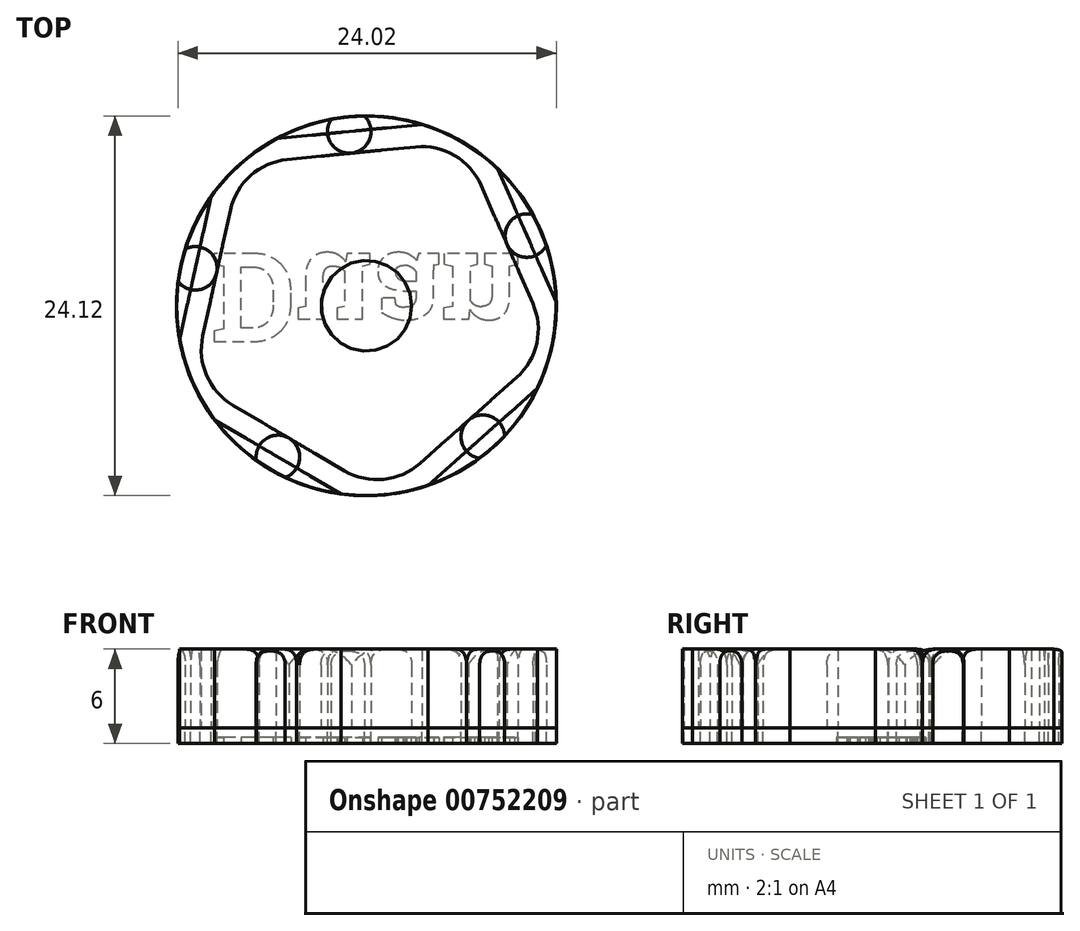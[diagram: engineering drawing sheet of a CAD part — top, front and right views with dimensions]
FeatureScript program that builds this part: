
annotation { "Feature Type Name" : "Feature", "Feature Type Description" : "" }
export const myFeature = defineFeature(function(context is Context, id is Id, definition is map)
    precondition{}
    {
        {
            var Q0;
            Q0=qCreatedBy(makeId("Top.planeOp"),FACE);
            var sketch = newSketch(context, id + "F0", { "sketchPlane" : qUnion([Q0])});
            skCircle(sketch, "E0", {"center": v(-4.76, 4.72) * mm, "radius": 4.1 * mm});
            skCircle(sketch, "E1.1.0", {"center": v(-6.51, -3.29) * mm, "radius": 4.1 * mm});
            skCircle(sketch, "E1.2.0", {"center": v(0.56, -7.43) * mm, "radius": 4.1 * mm});
            skCircle(sketch, "E1.3.0", {"center": v(6.7, -1.99) * mm, "radius": 4.1 * mm});
            skCircle(sketch, "E1.4.0", {"center": v(3.4, 5.53) * mm, "radius": 4.1 * mm});
            skPoint(sketch, "E1.center", {"position": v(-0.12, -0.5) * mm});
            skCircle(sketch, "E2", {"center": v(-0.12, -0.5) * mm, "radius": 12.06 * mm});
            skLineSegment(sketch, "E3", {"start": v(5.82, 8.84) * mm, "end": v(6.43, 9.63) * mm, "construction": true});
            skCircle(sketch, "E4", {"center": v(-0.12, -0.5) * mm, "radius": 2.88 * mm});
            skLineSegment(sketch, "E5", {"start": v(-8.58, -6.83) * mm, "end": v(-1.5, -10.97) * mm});
            skLineSegment(sketch, "E6", {"start": v(-9.76, -7.74) * mm, "end": v(-1.73, -12.44) * mm});
            skLineSegment(sketch, "E7.1.0", {"start": v(3.8, -11.9) * mm, "end": v(10.75, -5.72) * mm});
            skLineSegment(sketch, "E7.1.1", {"start": v(3.29, -10.5) * mm, "end": v(9.42, -5.05) * mm});
            skLineSegment(sketch, "E7.2.0", {"start": v(11.93, -0.3) * mm, "end": v(8.2, 8.23) * mm});
            skLineSegment(sketch, "E7.2.1", {"start": v(10.45, -0.34) * mm, "end": v(7.16, 7.17) * mm});
            skLineSegment(sketch, "E7.3.0", {"start": v(3.42, 11.04) * mm, "end": v(-5.84, 10.12) * mm});
            skLineSegment(sketch, "E7.3.1", {"start": v(3, 9.6) * mm, "end": v(-5.16, 8.8) * mm});
            skLineSegment(sketch, "E7.4.0", {"start": v(-10, 6.43) * mm, "end": v(-11.98, -2.66) * mm});
            skLineSegment(sketch, "E7.4.1", {"start": v(-8.76, 5.6) * mm, "end": v(-10.52, -2.41) * mm});
            skCircle(sketch, "E8", {"center": v(-5.75, -10.1) * mm, "radius": 1.38 * mm});
            skCircle(sketch, "E9.1.0", {"center": v(7.27, -8.8) * mm, "radius": 1.38 * mm});
            skCircle(sketch, "E9.2.0", {"center": v(10.07, 3.97) * mm, "radius": 1.38 * mm});
            skCircle(sketch, "E9.3.0", {"center": v(-1.21, 10.58) * mm, "radius": 1.38 * mm});
            skCircle(sketch, "E9.4.0", {"center": v(-10.99, 1.89) * mm, "radius": 1.38 * mm});
            skSolve(sketch);
        }
        {
            var Q0;
            {var subQ0=sQuery(id+"F0.wireOp",EDGE,"E8");var subQ1=sQuery(id+"F0.wireOp",EDGE,"E2");var subQ2=makeQuery(id+"F0.imprint","INTERSECT",VERTEX,{"disambiguationData":[OD(0.0)],"derivedFrom":[subQ1,subQ0]});Q0=makeQuery(id+"F0.imprint","IMPRINT",FACE,{"disambiguationData":[TD([[makeQuery(id+"F0.imprint","IMPRINT",EDGE,{"disambiguationData":[TD([[subQ2,-1.0]])],"derivedFrom":subQ1}),1.0]])]});}
            var Q1;
            {var subQ5=sQuery(id+"F0.wireOp",EDGE,"E7.1.1");var subQ6=sQuery(id+"F0.wireOp",EDGE,"E1.3.0");var subQ7=makeQuery(id+"F0.imprint","INTERSECT",VERTEX,{"derivedFrom":[subQ6,subQ5]});Q1=makeQuery(id+"F0.imprint","IMPRINT",FACE,{"disambiguationData":[TD([[makeQuery(id+"F0.imprint","IMPRINT",EDGE,{"disambiguationData":[TD([[subQ7,-1.0]])],"derivedFrom":subQ6}),-1.0]])]});}
            var Q2;
            {var subQ0=sQuery(id+"F0.wireOp",EDGE,"E7.1.1");var subQ1=sQuery(id+"F0.wireOp",EDGE,"E1.2.0");var subQ2=makeQuery(id+"F0.imprint","INTERSECT",VERTEX,{"derivedFrom":[subQ1,subQ0]});Q2=makeQuery(id+"F0.imprint","IMPRINT",FACE,{"disambiguationData":[TD([[makeQuery(id+"F0.imprint","IMPRINT",EDGE,{"disambiguationData":[TD([[subQ2,-1.0]])],"derivedFrom":subQ1}),-1.0]])]});}
            var Q3;
            {var subQ0=sQuery(id+"F0.wireOp",EDGE,"E4");var subQ4=makeQuery(id+"F0.imprint","INTERSECT",VERTEX,{"derivedFrom":[sQuery(id+"F0.wireOp",EDGE,"E0"),subQ0]});Q3=makeQuery(id+"F0.imprint","IMPRINT",FACE,{"disambiguationData":[TD([[makeQuery(id+"F0.imprint","IMPRINT",EDGE,{"disambiguationData":[TD([[subQ4,1.0]])],"derivedFrom":subQ0}),1.0]])]});}
            var Q4;
            {var subQ0=sQuery(id+"F0.wireOp",EDGE,"E9.4.0");var subQ1=sQuery(id+"F0.wireOp",EDGE,"E7.4.0");var subQ2=makeQuery(id+"F0.imprint","INTERSECT",VERTEX,{"disambiguationData":[OD(0.0)],"derivedFrom":[subQ1,subQ0]});Q4=makeQuery(id+"F0.imprint","IMPRINT",FACE,{"disambiguationData":[TD([[makeQuery(id+"F0.imprint","IMPRINT",EDGE,{"disambiguationData":[TD([[subQ2,-1.0]])],"derivedFrom":subQ1}),1.0]])]});}
            var Q5;
            {var subQ0=sQuery(id+"F0.wireOp",EDGE,"E1.3.0");var subQ1=sQuery(id+"F0.wireOp",EDGE,"E1.2.0");var subQ2=makeQuery(id+"F0.imprint","INTERSECT",VERTEX,{"derivedFrom":[subQ1,subQ0]});Q5=makeQuery(id+"F0.imprint","IMPRINT",FACE,{"disambiguationData":[TD([[makeQuery(id+"F0.imprint","IMPRINT",EDGE,{"disambiguationData":[TD([[subQ2,-1.0]])],"derivedFrom":subQ1}),-1.0]])]});}
            var Q6;
            {var subQ0=sQuery(id+"F0.wireOp",EDGE,"E9.1.0");var subQ1=sQuery(id+"F0.wireOp",EDGE,"E2");var subQ2=makeQuery(id+"F0.imprint","INTERSECT",VERTEX,{"disambiguationData":[OD(0.0)],"derivedFrom":[subQ1,subQ0]});Q6=makeQuery(id+"F0.imprint","IMPRINT",FACE,{"disambiguationData":[TD([[makeQuery(id+"F0.imprint","IMPRINT",EDGE,{"disambiguationData":[TD([[subQ2,-1.0]])],"derivedFrom":subQ1}),1.0]])]});}
            var Q7;
            {var subQ0=sQuery(id+"F0.wireOp",EDGE,"E9.3.0");var subQ1=sQuery(id+"F0.wireOp",EDGE,"E2");var subQ2=makeQuery(id+"F0.imprint","INTERSECT",VERTEX,{"disambiguationData":[OD(0.0)],"derivedFrom":[subQ1,subQ0]});Q7=makeQuery(id+"F0.imprint","IMPRINT",FACE,{"disambiguationData":[TD([[makeQuery(id+"F0.imprint","IMPRINT",EDGE,{"disambiguationData":[TD([[subQ2,-1.0]])],"derivedFrom":subQ1}),1.0]])]});}
            var Q8;
            {var subQ0=sQuery(id+"F0.wireOp",EDGE,"E7.3.1");var subQ1=sQuery(id+"F0.wireOp",EDGE,"E0");var subQ2=makeQuery(id+"F0.imprint","INTERSECT",VERTEX,{"derivedFrom":[subQ1,subQ0]});Q8=makeQuery(id+"F0.imprint","IMPRINT",FACE,{"disambiguationData":[TD([[makeQuery(id+"F0.imprint","IMPRINT",EDGE,{"disambiguationData":[TD([[subQ2,-1.0]])],"derivedFrom":subQ1}),-1.0]])]});}
            var Q9;
            {var subQ0=sQuery(id+"F0.wireOp",EDGE,"E7.3.1");var subQ1=sQuery(id+"F0.wireOp",EDGE,"E0");var subQ2=makeQuery(id+"F0.imprint","INTERSECT",VERTEX,{"derivedFrom":[subQ1,subQ0]});Q9=makeQuery(id+"F0.imprint","IMPRINT",FACE,{"disambiguationData":[TD([[makeQuery(id+"F0.imprint","IMPRINT",EDGE,{"disambiguationData":[TD([[subQ2,1.0]])],"derivedFrom":subQ1}),-1.0]])]});}
            var Q10;
            {var subQ0=sQuery(id+"F0.wireOp",EDGE,"E9.2.0");var subQ1=sQuery(id+"F0.wireOp",EDGE,"E2");var subQ2=makeQuery(id+"F0.imprint","INTERSECT",VERTEX,{"disambiguationData":[OD(0.0)],"derivedFrom":[subQ1,subQ0]});Q10=makeQuery(id+"F0.imprint","IMPRINT",FACE,{"disambiguationData":[TD([[makeQuery(id+"F0.imprint","IMPRINT",EDGE,{"disambiguationData":[TD([[subQ2,-1.0]])],"derivedFrom":subQ1}),1.0]])]});}
            var Q11;
            {var subQ0=sQuery(id+"F0.wireOp",EDGE,"E1.2.0");var subQ1=sQuery(id+"F0.wireOp",EDGE,"E1.1.0");var subQ2=makeQuery(id+"F0.imprint","INTERSECT",VERTEX,{"derivedFrom":[subQ1,subQ0]});Q11=makeQuery(id+"F0.imprint","IMPRINT",FACE,{"disambiguationData":[TD([[makeQuery(id+"F0.imprint","IMPRINT",EDGE,{"disambiguationData":[TD([[subQ2,-1.0]])],"derivedFrom":subQ1}),-1.0]])]});}
            var Q12;
            {var subQ0=sQuery(id+"F0.wireOp",EDGE,"E1.2.0");var subQ4=makeQuery(id+"F0.imprint","INTERSECT",VERTEX,{"derivedFrom":[subQ0,sQuery(id+"F0.wireOp",EDGE,"E5")]});Q12=makeQuery(id+"F0.imprint","IMPRINT",FACE,{"disambiguationData":[TD([[makeQuery(id+"F0.imprint","IMPRINT",EDGE,{"disambiguationData":[TD([[subQ4,1.0]])],"derivedFrom":subQ0}),1.0]])]});}
            var Q13;
            {var subQ0=sQuery(id+"F0.wireOp",EDGE,"E9.1.0");var subQ1=sQuery(id+"F0.wireOp",EDGE,"E7.1.0");var subQ2=makeQuery(id+"F0.imprint","INTERSECT",VERTEX,{"disambiguationData":[OD(0.0)],"derivedFrom":[subQ1,subQ0]});Q13=makeQuery(id+"F0.imprint","IMPRINT",FACE,{"disambiguationData":[TD([[makeQuery(id+"F0.imprint","IMPRINT",EDGE,{"disambiguationData":[TD([[subQ2,-1.0]])],"derivedFrom":subQ1}),1.0]])]});}
            var Q14;
            {var subQ0=sQuery(id+"F0.wireOp",EDGE,"E9.3.0");var subQ1=sQuery(id+"F0.wireOp",EDGE,"E7.3.0");var subQ2=makeQuery(id+"F0.imprint","INTERSECT",VERTEX,{"disambiguationData":[OD(0.0)],"derivedFrom":[subQ1,subQ0]});Q14=makeQuery(id+"F0.imprint","IMPRINT",FACE,{"disambiguationData":[TD([[makeQuery(id+"F0.imprint","IMPRINT",EDGE,{"disambiguationData":[TD([[subQ2,-1.0]])],"derivedFrom":subQ1}),1.0]])]});}
            var Q15;
            {var subQ0=sQuery(id+"F0.wireOp",EDGE,"E1.4.0");var subQ4=makeQuery(id+"F0.imprint","INTERSECT",VERTEX,{"derivedFrom":[subQ0,sQuery(id+"F0.wireOp",EDGE,"E7.2.1")]});Q15=makeQuery(id+"F0.imprint","IMPRINT",FACE,{"disambiguationData":[TD([[makeQuery(id+"F0.imprint","IMPRINT",EDGE,{"disambiguationData":[TD([[subQ4,1.0]])],"derivedFrom":subQ0}),1.0]])]});}
            var Q16;
            {var subQ7=sQuery(id+"F0.wireOp",EDGE,"E5");var subQ8=sQuery(id+"F0.wireOp",EDGE,"E1.2.0");var subQ9=makeQuery(id+"F0.imprint","INTERSECT",VERTEX,{"derivedFrom":[subQ8,subQ7]});Q16=makeQuery(id+"F0.imprint","IMPRINT",FACE,{"disambiguationData":[TD([[makeQuery(id+"F0.imprint","IMPRINT",EDGE,{"disambiguationData":[TD([[subQ9,-1.0]])],"derivedFrom":subQ8}),-1.0]])]});}
            var Q17;
            {var subQ0=sQuery(id+"F0.wireOp",EDGE,"E5");var subQ1=sQuery(id+"F0.wireOp",EDGE,"E1.1.0");var subQ2=makeQuery(id+"F0.imprint","INTERSECT",VERTEX,{"derivedFrom":[subQ1,subQ0]});Q17=makeQuery(id+"F0.imprint","IMPRINT",FACE,{"disambiguationData":[TD([[makeQuery(id+"F0.imprint","IMPRINT",EDGE,{"disambiguationData":[TD([[subQ2,-1.0]])],"derivedFrom":subQ1}),-1.0]])]});}
            var Q18;
            {var subQ0=sQuery(id+"F0.wireOp",EDGE,"E9.4.0");var subQ1=sQuery(id+"F0.wireOp",EDGE,"E2");var subQ2=makeQuery(id+"F0.imprint","INTERSECT",VERTEX,{"disambiguationData":[OD(0.0)],"derivedFrom":[subQ1,subQ0]});Q18=makeQuery(id+"F0.imprint","IMPRINT",FACE,{"disambiguationData":[TD([[makeQuery(id+"F0.imprint","IMPRINT",EDGE,{"disambiguationData":[TD([[subQ2,-1.0]])],"derivedFrom":subQ1}),1.0]])]});}
            var Q19;
            {var subQ0=sQuery(id+"F0.wireOp",EDGE,"E1.4.0");var subQ1=sQuery(id+"F0.wireOp",EDGE,"E0");var subQ2=makeQuery(id+"F0.imprint","INTERSECT",VERTEX,{"derivedFrom":[subQ1,subQ0]});Q19=makeQuery(id+"F0.imprint","IMPRINT",FACE,{"disambiguationData":[TD([[makeQuery(id+"F0.imprint","IMPRINT",EDGE,{"disambiguationData":[TD([[subQ2,1.0]])],"derivedFrom":subQ1}),-1.0]])]});}
            var Q20;
            {var subQ0=sQuery(id+"F0.wireOp",EDGE,"E1.1.0");var subQ1=sQuery(id+"F0.wireOp",EDGE,"E0");var subQ2=makeQuery(id+"F0.imprint","INTERSECT",VERTEX,{"derivedFrom":[subQ1,subQ0]});Q20=makeQuery(id+"F0.imprint","IMPRINT",FACE,{"disambiguationData":[TD([[makeQuery(id+"F0.imprint","IMPRINT",EDGE,{"disambiguationData":[TD([[subQ2,-1.0]])],"derivedFrom":subQ1}),-1.0]])]});}
            var Q21;
            {var subQ0=sQuery(id+"F0.wireOp",EDGE,"E7.2.1");var subQ1=sQuery(id+"F0.wireOp",EDGE,"E1.3.0");var subQ2=makeQuery(id+"F0.imprint","INTERSECT",VERTEX,{"derivedFrom":[subQ1,subQ0]});Q21=makeQuery(id+"F0.imprint","IMPRINT",FACE,{"disambiguationData":[TD([[makeQuery(id+"F0.imprint","IMPRINT",EDGE,{"disambiguationData":[TD([[subQ2,-1.0]])],"derivedFrom":subQ1}),-1.0]])]});}
            var Q22;
            {var subQ0=sQuery(id+"F0.wireOp",EDGE,"E1.1.0");var subQ4=makeQuery(id+"F0.imprint","INTERSECT",VERTEX,{"derivedFrom":[subQ0,sQuery(id+"F0.wireOp",EDGE,"E7.4.1")]});Q22=makeQuery(id+"F0.imprint","IMPRINT",FACE,{"disambiguationData":[TD([[makeQuery(id+"F0.imprint","IMPRINT",EDGE,{"disambiguationData":[TD([[subQ4,1.0]])],"derivedFrom":subQ0}),1.0]])]});}
            var Q23;
            {var subQ0=sQuery(id+"F0.wireOp",EDGE,"E7.2.1");var subQ1=sQuery(id+"F0.wireOp",EDGE,"E1.4.0");var subQ2=makeQuery(id+"F0.imprint","INTERSECT",VERTEX,{"derivedFrom":[subQ1,subQ0]});Q23=makeQuery(id+"F0.imprint","IMPRINT",FACE,{"disambiguationData":[TD([[makeQuery(id+"F0.imprint","IMPRINT",EDGE,{"disambiguationData":[TD([[subQ2,-1.0]])],"derivedFrom":subQ1}),-1.0]])]});}
            var Q24;
            {var subQ0=sQuery(id+"F0.wireOp",EDGE,"E8");var subQ1=sQuery(id+"F0.wireOp",EDGE,"E6");var subQ2=makeQuery(id+"F0.imprint","INTERSECT",VERTEX,{"disambiguationData":[OD(0.0)],"derivedFrom":[subQ1,subQ0]});Q24=makeQuery(id+"F0.imprint","IMPRINT",FACE,{"disambiguationData":[TD([[makeQuery(id+"F0.imprint","IMPRINT",EDGE,{"disambiguationData":[TD([[subQ2,-1.0]])],"derivedFrom":subQ1}),1.0]])]});}
            var Q25;
            {var subQ0=sQuery(id+"F0.wireOp",EDGE,"E9.2.0");var subQ1=sQuery(id+"F0.wireOp",EDGE,"E7.2.0");var subQ2=makeQuery(id+"F0.imprint","INTERSECT",VERTEX,{"disambiguationData":[OD(0.0)],"derivedFrom":[subQ1,subQ0]});Q25=makeQuery(id+"F0.imprint","IMPRINT",FACE,{"disambiguationData":[TD([[makeQuery(id+"F0.imprint","IMPRINT",EDGE,{"disambiguationData":[TD([[subQ2,-1.0]])],"derivedFrom":subQ1}),1.0]])]});}
            var Q26;
            {var subQ0=sQuery(id+"F0.wireOp",EDGE,"E1.3.0");var subQ4=makeQuery(id+"F0.imprint","INTERSECT",VERTEX,{"derivedFrom":[subQ0,sQuery(id+"F0.wireOp",EDGE,"E7.1.1")]});Q26=makeQuery(id+"F0.imprint","IMPRINT",FACE,{"disambiguationData":[TD([[makeQuery(id+"F0.imprint","IMPRINT",EDGE,{"disambiguationData":[TD([[subQ4,1.0]])],"derivedFrom":subQ0}),1.0]])]});}
            var Q27;
            {var subQ0=sQuery(id+"F0.wireOp",EDGE,"E7.4.1");var subQ1=sQuery(id+"F0.wireOp",EDGE,"E0");var subQ2=makeQuery(id+"F0.imprint","INTERSECT",VERTEX,{"derivedFrom":[subQ1,subQ0]});Q27=makeQuery(id+"F0.imprint","IMPRINT",FACE,{"disambiguationData":[TD([[makeQuery(id+"F0.imprint","IMPRINT",EDGE,{"disambiguationData":[TD([[subQ2,-1.0]])],"derivedFrom":subQ1}),-1.0]])]});}
            var Q28;
            {var subQ6=sQuery(id+"F0.wireOp",EDGE,"E1.1.0");var subQ10=sQuery(id+"F0.wireOp",EDGE,"E5");var subQ11=makeQuery(id+"F0.imprint","INTERSECT",VERTEX,{"derivedFrom":[subQ6,subQ10]});Q28=makeQuery(id+"F0.imprint","IMPRINT",FACE,{"disambiguationData":[TD([[makeQuery(id+"F0.imprint","IMPRINT",EDGE,{"disambiguationData":[TD([[subQ11,1.0]])],"derivedFrom":subQ6}),-1.0]])]});}
            var Q29;
            {var subQ0=sQuery(id+"F0.wireOp",EDGE,"E0");var subQ4=makeQuery(id+"F0.imprint","INTERSECT",VERTEX,{"derivedFrom":[subQ0,sQuery(id+"F0.wireOp",EDGE,"E7.3.1")]});Q29=makeQuery(id+"F0.imprint","IMPRINT",FACE,{"disambiguationData":[TD([[makeQuery(id+"F0.imprint","IMPRINT",EDGE,{"disambiguationData":[TD([[subQ4,1.0]])],"derivedFrom":subQ0}),1.0]])]});}
            var Q30;
            {var subQ0=sQuery(id+"F0.wireOp",EDGE,"E1.4.0");var subQ1=sQuery(id+"F0.wireOp",EDGE,"E1.3.0");var subQ2=makeQuery(id+"F0.imprint","INTERSECT",VERTEX,{"derivedFrom":[subQ1,subQ0]});Q30=makeQuery(id+"F0.imprint","IMPRINT",FACE,{"disambiguationData":[TD([[makeQuery(id+"F0.imprint","IMPRINT",EDGE,{"disambiguationData":[TD([[subQ2,-1.0]])],"derivedFrom":subQ1}),-1.0]])]});}
            extrude(context, id + "F1", {"entities" : qUnion([Q0, Q1, Q2, Q3, Q4, Q5, Q6, Q7, Q8, Q9, Q10, Q11, Q12, Q13, Q14, Q15, Q16, Q17, Q18, Q19, Q20, Q21, Q22, Q23, Q24, Q25, Q26, Q27, Q28, Q29, Q30]), "depth" : -1 * mm, "offsetDistance" : 25 * mm});
        }
        {
            var Q0;
            {var subQ0=sQuery(id+"F0.wireOp",EDGE,"E9.4.0");var subQ1=sQuery(id+"F0.wireOp",EDGE,"E7.4.0");var subQ2=makeQuery(id+"F0.imprint","INTERSECT",VERTEX,{"disambiguationData":[OD(0.0)],"derivedFrom":[subQ1,subQ0]});Q0=makeQuery(id+"F0.imprint","IMPRINT",FACE,{"disambiguationData":[TD([[makeQuery(id+"F0.imprint","IMPRINT",EDGE,{"disambiguationData":[TD([[subQ2,-1.0]])],"derivedFrom":subQ1}),1.0]])]});}
            var Q1;
            {var subQ0=sQuery(id+"F0.wireOp",EDGE,"E4");var subQ4=makeQuery(id+"F0.imprint","INTERSECT",VERTEX,{"derivedFrom":[sQuery(id+"F0.wireOp",EDGE,"E0"),subQ0]});Q1=makeQuery(id+"F0.imprint","IMPRINT",FACE,{"disambiguationData":[TD([[makeQuery(id+"F0.imprint","IMPRINT",EDGE,{"disambiguationData":[TD([[subQ4,1.0]])],"derivedFrom":subQ0}),1.0]])]});}
            var Q2;
            {var subQ0=sQuery(id+"F0.wireOp",EDGE,"E9.2.0");var subQ1=sQuery(id+"F0.wireOp",EDGE,"E7.2.0");var subQ2=makeQuery(id+"F0.imprint","INTERSECT",VERTEX,{"disambiguationData":[OD(0.0)],"derivedFrom":[subQ1,subQ0]});Q2=makeQuery(id+"F0.imprint","IMPRINT",FACE,{"disambiguationData":[TD([[makeQuery(id+"F0.imprint","IMPRINT",EDGE,{"disambiguationData":[TD([[subQ2,-1.0]])],"derivedFrom":subQ1}),1.0]])]});}
            var Q3;
            {var subQ0=sQuery(id+"F0.wireOp",EDGE,"E9.3.0");var subQ1=sQuery(id+"F0.wireOp",EDGE,"E7.3.0");var subQ2=makeQuery(id+"F0.imprint","INTERSECT",VERTEX,{"disambiguationData":[OD(0.0)],"derivedFrom":[subQ1,subQ0]});Q3=makeQuery(id+"F0.imprint","IMPRINT",FACE,{"disambiguationData":[TD([[makeQuery(id+"F0.imprint","IMPRINT",EDGE,{"disambiguationData":[TD([[subQ2,-1.0]])],"derivedFrom":subQ1}),1.0]])]});}
            var Q4;
            {var subQ0=sQuery(id+"F0.wireOp",EDGE,"E9.4.0");var subQ1=sQuery(id+"F0.wireOp",EDGE,"E2");var subQ2=makeQuery(id+"F0.imprint","INTERSECT",VERTEX,{"disambiguationData":[OD(0.0)],"derivedFrom":[subQ1,subQ0]});Q4=makeQuery(id+"F0.imprint","IMPRINT",FACE,{"disambiguationData":[TD([[makeQuery(id+"F0.imprint","IMPRINT",EDGE,{"disambiguationData":[TD([[subQ2,-1.0]])],"derivedFrom":subQ1}),1.0]])]});}
            var Q5;
            {var subQ0=sQuery(id+"F0.wireOp",EDGE,"E9.3.0");var subQ1=sQuery(id+"F0.wireOp",EDGE,"E2");var subQ2=makeQuery(id+"F0.imprint","INTERSECT",VERTEX,{"disambiguationData":[OD(0.0)],"derivedFrom":[subQ1,subQ0]});Q5=makeQuery(id+"F0.imprint","IMPRINT",FACE,{"disambiguationData":[TD([[makeQuery(id+"F0.imprint","IMPRINT",EDGE,{"disambiguationData":[TD([[subQ2,-1.0]])],"derivedFrom":subQ1}),1.0]])]});}
            var Q6;
            {var subQ0=sQuery(id+"F0.wireOp",EDGE,"E8");var subQ1=sQuery(id+"F0.wireOp",EDGE,"E2");var subQ2=makeQuery(id+"F0.imprint","INTERSECT",VERTEX,{"disambiguationData":[OD(0.0)],"derivedFrom":[subQ1,subQ0]});Q6=makeQuery(id+"F0.imprint","IMPRINT",FACE,{"disambiguationData":[TD([[makeQuery(id+"F0.imprint","IMPRINT",EDGE,{"disambiguationData":[TD([[subQ2,-1.0]])],"derivedFrom":subQ1}),1.0]])]});}
            var Q7;
            {var subQ0=sQuery(id+"F0.wireOp",EDGE,"E8");var subQ1=sQuery(id+"F0.wireOp",EDGE,"E6");var subQ2=makeQuery(id+"F0.imprint","INTERSECT",VERTEX,{"disambiguationData":[OD(0.0)],"derivedFrom":[subQ1,subQ0]});Q7=makeQuery(id+"F0.imprint","IMPRINT",FACE,{"disambiguationData":[TD([[makeQuery(id+"F0.imprint","IMPRINT",EDGE,{"disambiguationData":[TD([[subQ2,-1.0]])],"derivedFrom":subQ1}),1.0]])]});}
            var Q8;
            {var subQ0=sQuery(id+"F0.wireOp",EDGE,"E9.1.0");var subQ1=sQuery(id+"F0.wireOp",EDGE,"E7.1.0");var subQ2=makeQuery(id+"F0.imprint","INTERSECT",VERTEX,{"disambiguationData":[OD(0.0)],"derivedFrom":[subQ1,subQ0]});Q8=makeQuery(id+"F0.imprint","IMPRINT",FACE,{"disambiguationData":[TD([[makeQuery(id+"F0.imprint","IMPRINT",EDGE,{"disambiguationData":[TD([[subQ2,-1.0]])],"derivedFrom":subQ1}),1.0]])]});}
            var Q9;
            {var subQ0=sQuery(id+"F0.wireOp",EDGE,"E9.1.0");var subQ1=sQuery(id+"F0.wireOp",EDGE,"E2");var subQ2=makeQuery(id+"F0.imprint","INTERSECT",VERTEX,{"disambiguationData":[OD(0.0)],"derivedFrom":[subQ1,subQ0]});Q9=makeQuery(id+"F0.imprint","IMPRINT",FACE,{"disambiguationData":[TD([[makeQuery(id+"F0.imprint","IMPRINT",EDGE,{"disambiguationData":[TD([[subQ2,-1.0]])],"derivedFrom":subQ1}),1.0]])]});}
            var Q10;
            {var subQ0=sQuery(id+"F0.wireOp",EDGE,"E9.2.0");var subQ1=sQuery(id+"F0.wireOp",EDGE,"E2");var subQ2=makeQuery(id+"F0.imprint","INTERSECT",VERTEX,{"disambiguationData":[OD(0.0)],"derivedFrom":[subQ1,subQ0]});Q10=makeQuery(id+"F0.imprint","IMPRINT",FACE,{"disambiguationData":[TD([[makeQuery(id+"F0.imprint","IMPRINT",EDGE,{"disambiguationData":[TD([[subQ2,-1.0]])],"derivedFrom":subQ1}),1.0]])]});}
            extrude(context, id + "F2", {"entities" : qUnion([Q0, Q1, Q2, Q3, Q4, Q5, Q6, Q7, Q8, Q9, Q10]), "depth" : 5 * mm, "offsetDistance" : 25 * mm});
        }
        {
            var Q0;
            Q0=makeQuery(id+"F1.opExtrude","CAP_FACE",FACE,{"disambiguationData":[OSD([sQuery(id+"F0.wireOp",EDGE,"E2"),sQuery(id+"F0.wireOp",EDGE,"E6"),sQuery(id+"F0.wireOp",EDGE,"E7.1.0"),sQuery(id+"F0.wireOp",EDGE,"E7.2.0"),sQuery(id+"F0.wireOp",EDGE,"E7.3.0"),sQuery(id+"F0.wireOp",EDGE,"E7.4.0"),sQuery(id+"F0.wireOp",EDGE,"E8"),sQuery(id+"F0.wireOp",EDGE,"E9.1.0"),sQuery(id+"F0.wireOp",EDGE,"E9.2.0"),sQuery(id+"F0.wireOp",EDGE,"E9.3.0"),sQuery(id+"F0.wireOp",EDGE,"E9.4.0")])],"isStart":false});
            var sketch = newSketch(context, id + "F3", { "sketchPlane" : qUnion([Q0])});
            skText(sketch, "E10", { "text": "Duan", "fontName": "RobotoSlab-Bold.ttf"});
            const initialGuessF3  = {"E10": [-0.01, -0.00283, 1, 0, 0.00566]};
            skSetInitialGuess(sketch, initialGuessF3);
            skSolve(sketch);
        }
        {
            var Q0;
            Q0=makeQuery(id+"F3.imprint","IMPRINT",FACE,{"disambiguationData":[TD([[makeQuery(id+"F3.imprint","IMPRINT",EDGE,{"derivedFrom":sQuery(id+"F3.wireOp",EDGE,"E10.sketch_text.stroke-0")}),-1.0]])]});
            var Q1;
            Q1=makeQuery(id+"F3.imprint","IMPRINT",FACE,{"disambiguationData":[TD([[makeQuery(id+"F3.imprint","IMPRINT",EDGE,{"derivedFrom":sQuery(id+"F3.wireOp",EDGE,"E10.sketch_text.stroke-21")}),-1.0]])]});
            var Q2;
            Q2=makeQuery(id+"F3.imprint","IMPRINT",FACE,{"disambiguationData":[TD([[makeQuery(id+"F3.imprint","IMPRINT",EDGE,{"derivedFrom":sQuery(id+"F3.wireOp",EDGE,"E10.sketch_text.stroke-45")}),-1.0]])]});
            var Q3;
            Q3=makeQuery(id+"F3.imprint","IMPRINT",FACE,{"disambiguationData":[TD([[makeQuery(id+"F3.imprint","IMPRINT",EDGE,{"derivedFrom":sQuery(id+"F3.wireOp",EDGE,"E10.sketch_text.stroke-80")}),-1.0]])]});
            extrude(context, id + "F4", {"entities" : qUnion([Q0, Q1, Q2, Q3]), "operationType" : NewBodyOperationType.REMOVE, "oppositeDirection" : true, "depth" : 0.4 * mm, "offsetDistance" : 25 * mm});
        }
        {
            var Q0;
            Q0=makeQuery(id+"F2.opExtrude","CAP_EDGE",EDGE,{"disambiguationData":[OSD([sQuery(id+"F0.wireOp",EDGE,"E4")])],"isStart":false});
            var Q1;
            Q1=makeQuery(id+"F2.opExtrude","CAP_EDGE",EDGE,{"disambiguationData":[OSD([sQuery(id+"F0.wireOp",EDGE,"E8")])],"isStart":false});
            var Q2;
            Q2=makeQuery(id+"F2.opExtrude","CAP_EDGE",EDGE,{"disambiguationData":[OSD([sQuery(id+"F0.wireOp",EDGE,"E9.1.0")])],"isStart":false});
            var Q3;
            Q3=makeQuery(id+"F2.opExtrude","CAP_EDGE",EDGE,{"disambiguationData":[OSD([sQuery(id+"F0.wireOp",EDGE,"E9.2.0")])],"isStart":false});
            var Q4;
            Q4=makeQuery(id+"F2.opExtrude","CAP_EDGE",EDGE,{"disambiguationData":[OSD([sQuery(id+"F0.wireOp",EDGE,"E9.3.0")])],"isStart":false});
            var Q5;
            Q5=makeQuery(id+"F2.opExtrude","CAP_EDGE",EDGE,{"disambiguationData":[OSD([sQuery(id+"F0.wireOp",EDGE,"E9.4.0")])],"isStart":false});
            fillet(context, id + "F5", {"entities" : qUnion([Q0, Q1, Q2, Q3, Q4, Q5]), "radius" : 1 * mm, "tangentPropagation" : true, "rho" : 0.5, "crossSection" : FilletCrossSection.CONIC, "allowEdgeOverflow" : false});
        }
    });
